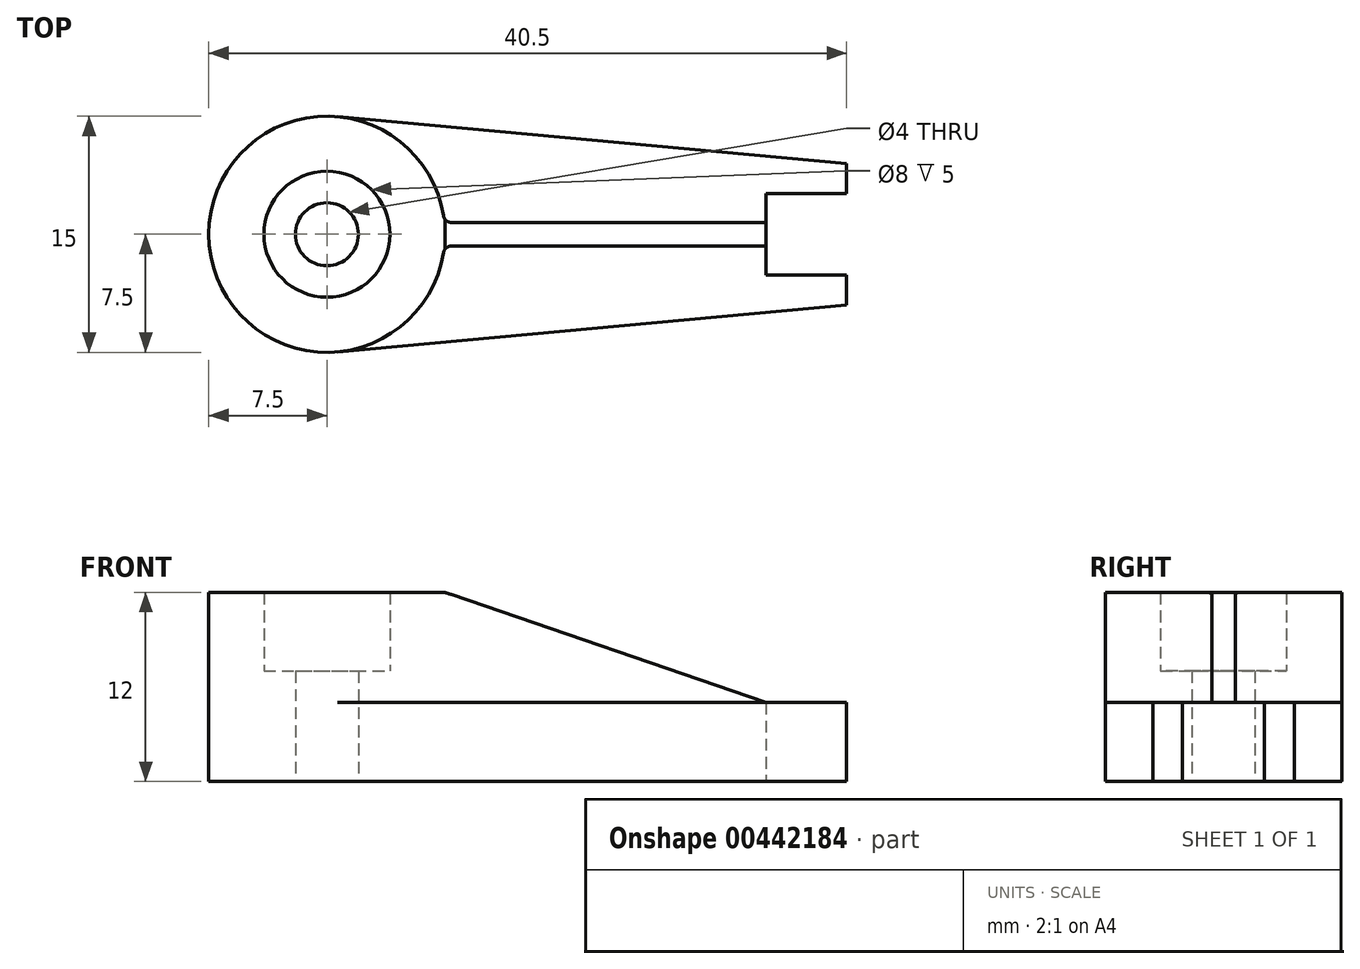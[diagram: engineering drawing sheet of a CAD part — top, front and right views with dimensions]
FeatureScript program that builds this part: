
annotation { "Feature Type Name" : "Feature", "Feature Type Description" : "" }
export const myFeature = defineFeature(function(context is Context, id is Id, definition is map)
    precondition{}
    {
        {
            var Q0;
            Q0=qCreatedBy(makeId("Top.planeOp"),FACE);
            var sketch = newSketch(context, id + "F0", { "sketchPlane" : qUnion([Q0])});
            skCircle(sketch, "E0", {"center": v(0, 0) * mm, "radius": 7.5 * mm});
            skLineSegment(sketch, "E1", {"start": v(0.69, 7.47) * mm, "end": v(33, 4.5) * mm});
            skLineSegment(sketch, "E2", {"start": v(0.69, -7.47) * mm, "end": v(33, -4.5) * mm});
            skLineSegment(sketch, "E3", {"start": v(33, 4.5) * mm, "end": v(33, 2.6) * mm});
            skLineSegment(sketch, "E4", {"start": v(33, 2.6) * mm, "end": v(27.9, 2.6) * mm});
            skLineSegment(sketch, "E5", {"start": v(27.9, 2.6) * mm, "end": v(27.9, -2.6) * mm});
            skLineSegment(sketch, "E6", {"start": v(27.9, -2.6) * mm, "end": v(33, -2.6) * mm});
            skLineSegment(sketch, "E7", {"start": v(33, -2.6) * mm, "end": v(33, -4.5) * mm});
            skLineSegment(sketch, "E8", {"start": v(33, 4.5) * mm, "end": v(27.02, 4.5) * mm, "construction": true});
            skSolve(sketch);
        }
        {
            var Q0;
            {var subQ0=sQuery(id+"F0.wireOp",EDGE,"E0");var subQ1=makeQuery(id+"F0.imprint","INTERSECT",VERTEX,{"derivedFrom":[subQ0,sQuery(id+"F0.wireOp",EDGE,"E1")]});Q0=makeQuery(id+"F0.imprint","IMPRINT",FACE,{"disambiguationData":[TD([[makeQuery(id+"F0.imprint","IMPRINT",EDGE,{"disambiguationData":[TD([[subQ1,-1.0]])],"derivedFrom":subQ0}),1.0]])]});}
            extrude(context, id + "F1", {"entities" : qUnion([Q0]), "depth" : 12 * mm});
        }
        {
            var Q0;
            {var subQ1=sQuery(id+"F0.wireOp",EDGE,"E1");Q0=makeQuery(id+"F0.imprint","IMPRINT",FACE,{"disambiguationData":[TD([[makeQuery(id+"F0.imprint","IMPRINT",EDGE,{"derivedFrom":subQ1}),-1.0]])]});}
            extrude(context, id + "F2", {"entities" : qUnion([Q0]), "operationType" : NewBodyOperationType.ADD, "depth" : 5 * mm});
        }
        {
            var Q0;
            Q0=qCreatedBy(makeId("Front.planeOp"),FACE);
            var sketch = newSketch(context, id + "F3", { "sketchPlane" : qUnion([Q0])});
            skLineSegment(sketch, "E9.0", {"start": v(0.69, 12) * mm, "end": v(7.5, 12) * mm});
            skLineSegment(sketch, "E10", {"start": v(0.69, 5) * mm, "end": v(0.69, 12) * mm});
            skLineSegment(sketch, "E11", {"start": v(0.69, 12) * mm, "end": v(0.69, 12) * mm});
            skPoint(sketch, "E12.orphan", {"position": v(-7.5, 12) * mm});
            skPoint(sketch, "E13.0", {"position": v(27.9, 5) * mm});
            skLineSegment(sketch, "E14", {"start": v(7.5, 12) * mm, "end": v(27.9, 5) * mm});
            skLineSegment(sketch, "E15", {"start": v(0.69, 5) * mm, "end": v(27.9, 5) * mm});
            skSolve(sketch);
        }
        {
            var Q0;
            Q0=makeQuery(id+"F3.imprint","IMPRINT",FACE,{"disambiguationData":[TD([[makeQuery(id+"F3.imprint","IMPRINT",EDGE,{"derivedFrom":sQuery(id+"F3.wireOp",EDGE,"E10")}),-1.0]])]});
            extrude(context, id + "F4", {"entities" : qUnion([Q0]), "operationType" : NewBodyOperationType.ADD, "depth" : 1.5 * mm, "symmetric" : true});
        }
        {
            var Q0;
            Q0=makeQuery(id+"F4.boolean.opBoolean","MERGE",FACE,{"derivedFrom":[makeQuery(id+"F1.opExtrude","CAP_FACE",FACE,{"disambiguationData":[OSD([sQuery(id+"F0.wireOp",EDGE,"E0")])],"isStart":false}),makeQuery(id+"F4.opExtrude","SWEPT_FACE",FACE,{"disambiguationData":[OSD([sQuery(id+"F3.wireOp",EDGE,"E9.0")])]})]});
            var sketch = newSketch(context, id + "F5", { "sketchPlane" : qUnion([Q0])});
            skPoint(sketch, "E16.0", {"position": v(0, 0) * mm});
            skSolve(sketch);
        }
        {
            var Q0;
            Q0=sQuery(id+"F5.wireOp",VERTEX,"E16.0");
            var Q1;
            Q1=makeQuery(id+"F1.opExtrude","SWEPT_BODY",BODY,{"disambiguationData":[OSD([sQuery(id+"F0.wireOp",EDGE,"E0")])]});
            hole(context, id + "F6", {"style" : HoleStyle.C_BORE, "endStyle" : HoleEndStyle.THROUGH, "holeDiameter" : 4 * mm, "cBoreDiameter" : 8 * mm, "cBoreDepth" : 5 * mm, "isTappedThrough" : true, "tappedDepth" : 12 * mm, "tapClearance" : 3, "locations" : qUnion([Q0]), "scope" : qUnion([Q1]), "startStyle" : HoleStartStyle.PART});
        }
        {
            var Q0;
            Q0=makeQuery(id+"F4.opExtrude","CAP_EDGE",EDGE,{"disambiguationData":[OSD([sQuery(id+"F3.wireOp",EDGE,"E15")])],"isStart":false});
            var Q1;
            {var subQ0=sQuery(id+"F0.wireOp",EDGE,"E0");var subQ1=sQuery(id+"F0.wireOp",EDGE,"E2");Q1=makeQuery(id+"F4.boolean.opBoolean","SPLIT",EDGE,{"disambiguationData":[TD([makeQuery(id+"F2.opExtrude","SWEPT_FACE",FACE,{"disambiguationData":[OSD([subQ1])]})])],"derivedFrom":makeQuery(id+"F2.opExtrude","CAP_EDGE",EDGE,{"disambiguationData":[OSD([subQ0])],"isStart":false})});}
            var Q2;
            Q2=makeQuery(id+"F4.boolean.opBoolean","INTERSECT",EDGE,{"derivedFrom":[makeQuery(id+"F1.opExtrude","SWEPT_FACE",FACE,{"disambiguationData":[OSD([sQuery(id+"F0.wireOp",EDGE,"E0")])]}),makeQuery(id+"F4.opExtrude","CAP_FACE",FACE,{"disambiguationData":[OSD([sQuery(id+"F3.wireOp",EDGE,"E10"),sQuery(id+"F3.wireOp",EDGE,"E9.0"),sQuery(id+"F3.wireOp",EDGE,"E14"),sQuery(id+"F3.wireOp",EDGE,"E15")])],"isStart":false})]});
            var Q3;
            Q3=makeQuery(id+"F4.opExtrude","CAP_EDGE",EDGE,{"disambiguationData":[OSD([sQuery(id+"F3.wireOp",EDGE,"E15")])],"isStart":true});
            var Q4;
            {var subQ0=sQuery(id+"F0.wireOp",EDGE,"E0");var subQ1=sQuery(id+"F0.wireOp",EDGE,"E1");Q4=makeQuery(id+"F4.boolean.opBoolean","SPLIT",EDGE,{"disambiguationData":[TD([makeQuery(id+"F2.opExtrude","SWEPT_FACE",FACE,{"disambiguationData":[OSD([subQ1])]})])],"derivedFrom":makeQuery(id+"F2.opExtrude","CAP_EDGE",EDGE,{"disambiguationData":[OSD([subQ0])],"isStart":false})});}
            var Q5;
            Q5=makeQuery(id+"F4.boolean.opBoolean","INTERSECT",EDGE,{"derivedFrom":[makeQuery(id+"F1.opExtrude","SWEPT_FACE",FACE,{"disambiguationData":[OSD([sQuery(id+"F0.wireOp",EDGE,"E0")])]}),makeQuery(id+"F4.opExtrude","CAP_FACE",FACE,{"disambiguationData":[OSD([sQuery(id+"F3.wireOp",EDGE,"E10"),sQuery(id+"F3.wireOp",EDGE,"E9.0"),sQuery(id+"F3.wireOp",EDGE,"E14"),sQuery(id+"F3.wireOp",EDGE,"E15")])],"isStart":true})]});
            fillet(context, id + "F7", {"entities" : qUnion([Q0, Q1, Q2, Q3, Q4, Q5]), "radius" : .5 * mm, "tangentPropagation" : true, "allowEdgeOverflow" : false});
        }
    });
